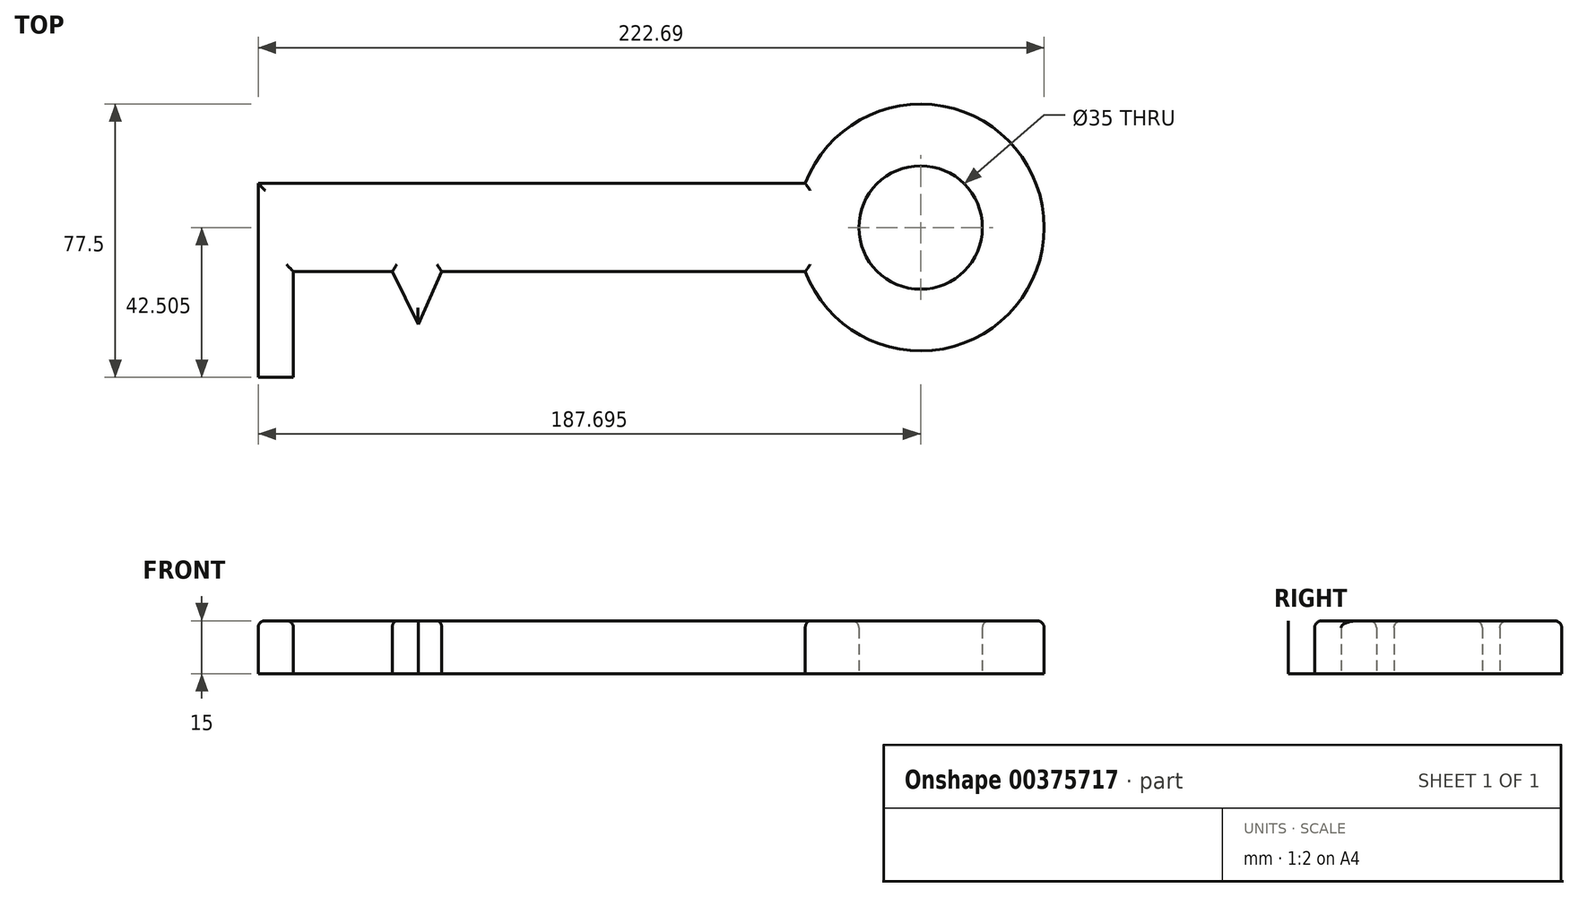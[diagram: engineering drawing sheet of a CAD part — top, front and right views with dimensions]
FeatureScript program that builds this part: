
annotation { "Feature Type Name" : "Feature", "Feature Type Description" : "" }
export const myFeature = defineFeature(function(context is Context, id is Id, definition is map)
    precondition{}
    {
        {
            var Q0;
            Q0=qCreatedBy(makeId("Top.planeOp"),FACE);
            var sketch = newSketch(context, id + "F0", { "sketchPlane" : qUnion([Q0])});
            skLineSegment(sketch, "E0.bottom", {"start": v(-109.05, 7.71) * mm, "end": v(45.95, 7.71) * mm});
            skLineSegment(sketch, "E0.top", {"start": v(-109.05, 32.71) * mm, "end": v(45.95, 32.71) * mm});
            skLineSegment(sketch, "E0.left", {"start": v(-109.05, 7.71) * mm, "end": v(-109.05, 32.71) * mm});
            skLineSegment(sketch, "E0.right", {"start": v(45.95, 7.71) * mm, "end": v(45.95, 32.71) * mm});
            skLineSegment(sketch, "E1.bottom", {"start": v(-99.05, -22.29) * mm, "end": v(-109.05, -22.29) * mm});
            skLineSegment(sketch, "E1.top", {"start": v(-99.05, 7.71) * mm, "end": v(-109.05, 7.71) * mm});
            skLineSegment(sketch, "E1.left", {"start": v(-99.05, -22.29) * mm, "end": v(-99.05, 7.71) * mm});
            skLineSegment(sketch, "E1.right", {"start": v(-109.05, -22.29) * mm, "end": v(-109.05, 7.71) * mm});
            skLineSegment(sketch, "E2.bottom", {"start": v(-89.05, 7.71) * mm, "end": v(-81.05, 7.71) * mm});
            skLineSegment(sketch, "E2.top", {"start": v(-89.05, -7.29) * mm, "end": v(-81.05, -7.29) * mm});
            skLineSegment(sketch, "E2.left", {"start": v(-89.05, 7.71) * mm, "end": v(-89.05, -7.29) * mm});
            skLineSegment(sketch, "E2.right", {"start": v(-81.05, 7.71) * mm, "end": v(-81.05, -7.29) * mm});
            skLineSegment(sketch, "E3", {"start": v(-71.05, 7.71) * mm, "end": v(-63.7, -7.29) * mm});
            skLineSegment(sketch, "E4", {"start": v(-57.05, 7.71) * mm, "end": v(-63.7, -7.29) * mm});
            skArc(sketch, "E5", {"start": v(45.95, 7.71) * mm, "mid": v(113.64, 20.21) * mm, "end": v(45.95, 32.71) * mm});
            skCircle(sketch, "E6", {"center": v(78.64, 20.21) * mm, "radius": 17.5 * mm});
            skSolve(sketch);
        }
        {
            var Q0;
            Q0=makeQuery(id+"F0.imprint","IMPRINT",FACE,{"disambiguationData":[TD([[makeQuery(id+"F0.imprint","IMPRINT",EDGE,{"derivedFrom":sQuery(id+"F0.wireOp",EDGE,"E0.top")}),-1.0]])]});
            var Q1;
            Q1=makeQuery(id+"F0.imprint","IMPRINT",FACE,{"disambiguationData":[TD([[makeQuery(id+"F0.imprint","IMPRINT",EDGE,{"derivedFrom":sQuery(id+"F0.wireOp",EDGE,"E0.right")}),-1.0]])]});
            var Q2;
            Q2=makeQuery(id+"F0.imprint","IMPRINT",FACE,{"disambiguationData":[TD([[makeQuery(id+"F0.imprint","IMPRINT",EDGE,{"derivedFrom":sQuery(id+"F0.wireOp",EDGE,"E1.bottom")}),-1.0]])]});
            var Q3;
            Q3=makeQuery(id+"F0.imprint","IMPRINT",FACE,{"disambiguationData":[TD([[makeQuery(id+"F0.imprint","IMPRINT",EDGE,{"derivedFrom":sQuery(id+"F0.wireOp",EDGE,"E2.bottom")}),-1.0]])]});
            var Q4;
            {var subQ0=sQuery(id+"F0.wireOp",EDGE,"E3");Q4=makeQuery(id+"F0.imprint","IMPRINT",FACE,{"disambiguationData":[TD([[makeQuery(id+"F0.imprint","IMPRINT",EDGE,{"derivedFrom":subQ0}),1.0]])]});}
            extrude(context, id + "F1", {"entities" : qUnion([Q0, Q1, Q2, Q3, Q4]), "depth" : 15 * mm});
        }
        {
            var Q0;
            Q0=makeQuery(id+"F1.opExtrude","CAP_EDGE",EDGE,{"disambiguationData":[OSD([sQuery(id+"F0.wireOp",EDGE,"E0.left"),sQuery(id+"F0.wireOp",EDGE,"E1.right")])],"isStart":false});
            var Q1;
            Q1=makeQuery(id+"F1.opExtrude","CAP_EDGE",EDGE,{"disambiguationData":[OSD([sQuery(id+"F0.wireOp",EDGE,"E0.top")])],"isStart":false});
            var Q2;
            Q2=makeQuery(id+"F1.opExtrude","CAP_EDGE",EDGE,{"disambiguationData":[OSD([sQuery(id+"F0.wireOp",EDGE,"E1.left")])],"isStart":false});
            var Q3;
            {var subQ0=sQuery(id+"F0.wireOp",EDGE,"E0.bottom");Q3=makeQuery(id+"F1.opExtrude","CAP_EDGE",EDGE,{"disambiguationData":[OSD([subQ0]),TDD([makeQuery(id+"F0.imprint","IMPRINT",EDGE,{"disambiguationData":[TD([[makeQuery(id+"F0.imprint","INTERSECT",VERTEX,{"derivedFrom":[subQ0,sQuery(id+"F0.wireOp",EDGE,"E1.top"),sQuery(id+"F0.wireOp",EDGE,"E1.left")]}),-1.0]])],"derivedFrom":subQ0})])],"isStart":false});}
            var Q4;
            Q4=makeQuery(id+"F1.opExtrude","CAP_EDGE",EDGE,{"disambiguationData":[OSD([sQuery(id+"F0.wireOp",EDGE,"E2.top")])],"isStart":false});
            var Q5;
            {var subQ0=sQuery(id+"F0.wireOp",EDGE,"E0.bottom");Q5=makeQuery(id+"F1.opExtrude","CAP_EDGE",EDGE,{"disambiguationData":[OSD([subQ0]),TDD([makeQuery(id+"F0.imprint","IMPRINT",EDGE,{"disambiguationData":[TD([[makeQuery(id+"F0.imprint","INTERSECT",VERTEX,{"derivedFrom":[subQ0,sQuery(id+"F0.wireOp",EDGE,"E3")]}),1.0]])],"derivedFrom":subQ0})])],"isStart":false});}
            var Q6;
            Q6=makeQuery(id+"F1.opExtrude","CAP_EDGE",EDGE,{"disambiguationData":[OSD([sQuery(id+"F0.wireOp",EDGE,"E3")])],"isStart":false});
            var Q7;
            {var subQ0=sQuery(id+"F0.wireOp",EDGE,"E0.bottom");Q7=makeQuery(id+"F1.opExtrude","CAP_EDGE",EDGE,{"disambiguationData":[OSD([subQ0]),TDD([makeQuery(id+"F0.imprint","IMPRINT",EDGE,{"disambiguationData":[TD([[makeQuery(id+"F0.imprint","INTERSECT",VERTEX,{"derivedFrom":[subQ0,sQuery(id+"F0.wireOp",EDGE,"E4")]}),-1.0]])],"derivedFrom":subQ0})])],"isStart":false});}
            var Q8;
            Q8=makeQuery(id+"F1.opExtrude","CAP_EDGE",EDGE,{"disambiguationData":[OSD([sQuery(id+"F0.wireOp",EDGE,"E5")])],"isStart":false});
            var Q9;
            Q9=makeQuery(id+"F1.opExtrude","CAP_EDGE",EDGE,{"disambiguationData":[OSD([sQuery(id+"F0.wireOp",EDGE,"E6")])],"isStart":false});
            var Q10;
            Q10=makeQuery(id+"F1.opExtrude","CAP_EDGE",EDGE,{"disambiguationData":[OSD([sQuery(id+"F0.wireOp",EDGE,"E4")])],"isStart":false});
            var Q11;
            Q11=makeQuery(id+"F1.opExtrude","CAP_EDGE",EDGE,{"disambiguationData":[OSD([sQuery(id+"F0.wireOp",EDGE,"E2.right")])],"isStart":false});
            var Q12;
            Q12=makeQuery(id+"F1.opExtrude","CAP_EDGE",EDGE,{"disambiguationData":[OSD([sQuery(id+"F0.wireOp",EDGE,"E2.left")])],"isStart":false});
            fillet(context, id + "F2", {"entities" : qUnion([Q0, Q1, Q2, Q3, Q4, Q5, Q6, Q7, Q8, Q9, Q10, Q11, Q12]), "radius" : 2 * mm, "tangentPropagation" : true, "allowEdgeOverflow" : false});
        }
    });
